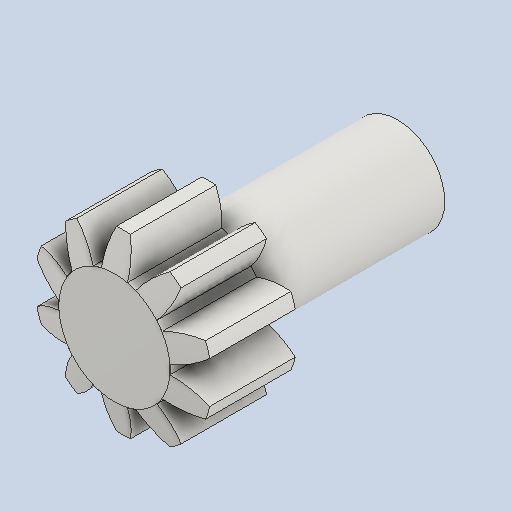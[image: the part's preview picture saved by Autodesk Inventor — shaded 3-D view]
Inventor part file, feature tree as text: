
AUTODESK INVENTOR PART (.ipt)
format: ipt  version: 2022 (Build 260153000, 153)  size: 544,768 bytes
history: native  units: mm (DEFAULTED — no unit token found)
features: sketch x6, extrude x4, plane x3, other x3, projected_geometry x2, revolve x1
ambient origin geometry x8: Origin, YZ Plane, XZ Plane, XY Plane, X Axis, Y Axis, Z Axis, Center Point
bodies: Solid1 (feature_tree)
feature tree (19):
  extrude  "Extrusion1"  Depth=6.35mm TaperAngle=0.0deg
  plane  "Work Plane1"
  plane  "Work Plane2"
  plane  "Work Plane3"
  other  "Spur Gear"
  extrude  "Extrusion2"  Depth=10.0mm TaperAngle=0.0deg
  extrude  "Extrusion3"  TaperAngle=0.0deg  [1 undecoded]
  revolve  "Revolution1"  [1 undecoded]
  extrude  "Extrusion4"  TaperAngle=0.0deg  [1 undecoded]
  sketch  "Sketch1"  dims[d0=11.961521mm d1=6.35mm d2=0.0mm]
  sketch  "Sketch2"  dims[d3=10.0mm d4=76.2mm d5=0.0mm]
  other  "Srf1"
  sketch  "Sketch3"  dims[d6=0.0mm d7=3.141593mm d9=0.0mm]
  sketch  "Sketch4"  dims[d14=0.0mm d15=23.753344mm]
  projected_geometry  "Projected Loop1"
  sketch  "Sketch5"  dims[d16=0.0mm d17=0.0mm]
  sketch  "Sketch6"  dims[d18=0.0mm d19=23.753344mm d20=3.325mm d22=0.0mm d23=0.0mm d24=6.35mm d25=12.7mm d26=0.0mm d27=15.0deg d28=90.0deg d29=2.0mm d30=0.0mm]
  projected_geometry  "Projected Loop2"
  other  "Pitch Diameter"
note: 3 required parameter values undecoded (feature->parameter linkage not recoverable at this tier; creation-order binding heuristic only, values carry confidence <= 0.55)